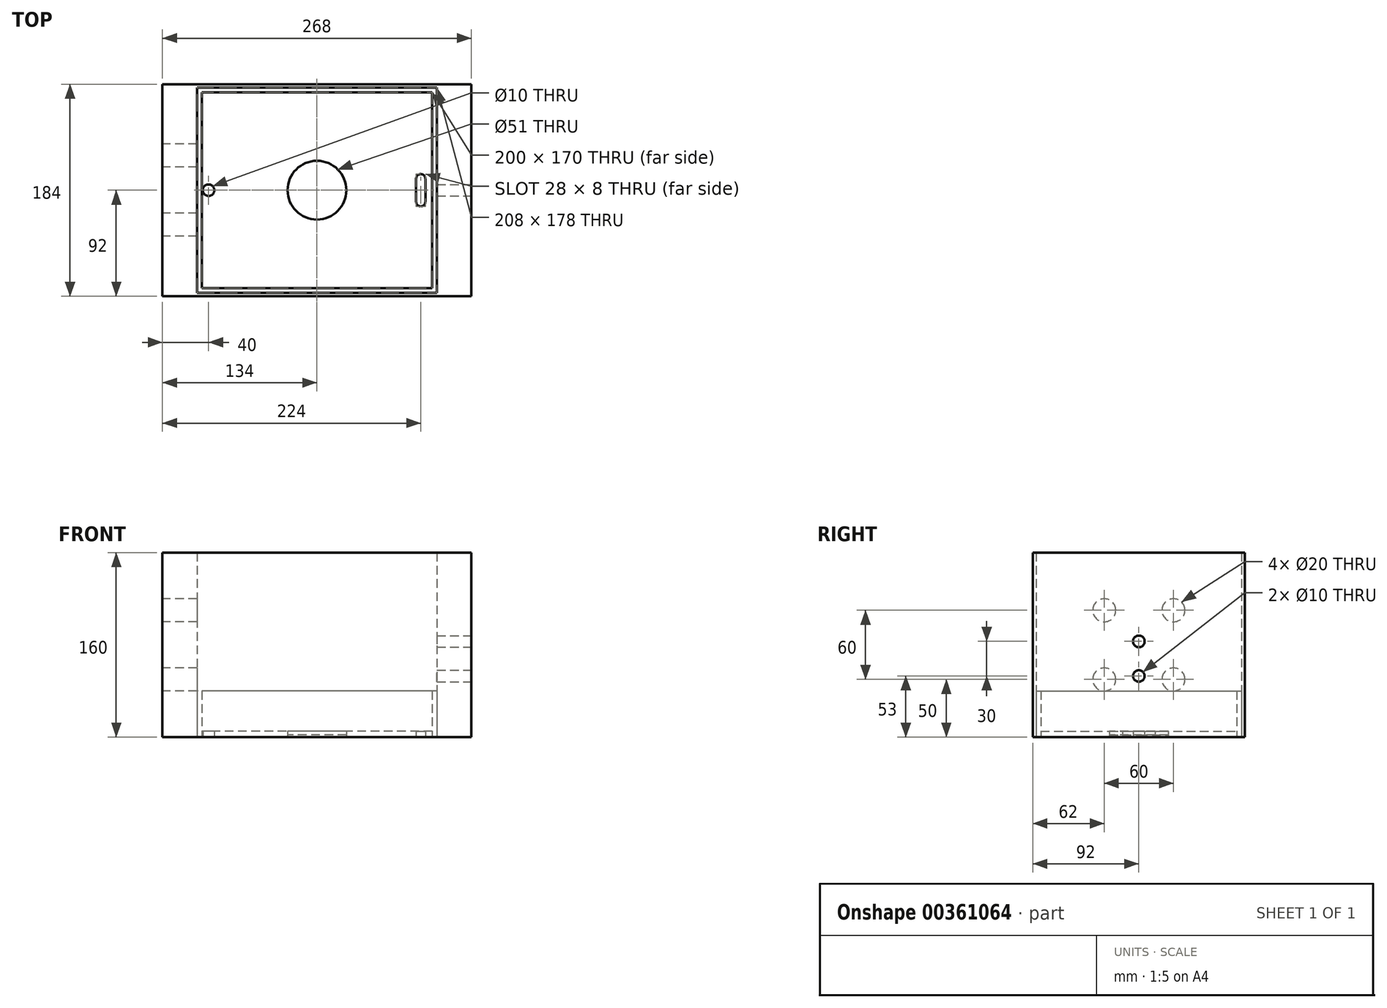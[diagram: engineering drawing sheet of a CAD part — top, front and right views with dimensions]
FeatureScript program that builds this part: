
annotation { "Feature Type Name" : "Feature", "Feature Type Description" : "" }
export const myFeature = defineFeature(function(context is Context, id is Id, definition is map)
    precondition{}
    {
        {
            var Q0;
            Q0=qCreatedBy(makeId("Top.planeOp"),FACE);
            var sketch = newSketch(context, id + "F0", { "sketchPlane" : qUnion([Q0])});
            skLineSegment(sketch, "E0.bottom", {"start": v(134, -92) * mm, "end": v(-134, -92) * mm});
            skLineSegment(sketch, "E0.top", {"start": v(134, 92) * mm, "end": v(-134, 92) * mm});
            skPoint(sketch, "E0.middle", {"position": v(0, 0) * mm});
            skCircle(sketch, "E1", {"center": v(0, 0) * mm, "radius": 25.5 * mm});
            skLineSegment(sketch, "E2.0", {"start": v(-100, -85) * mm, "end": v(-100, 85) * mm});
            skLineSegment(sketch, "E2.1", {"start": v(100, -85) * mm, "end": v(-100, -85) * mm});
            skLineSegment(sketch, "E2.2", {"start": v(100, -85) * mm, "end": v(100, 85) * mm});
            skLineSegment(sketch, "E2.3", {"start": v(100, 85) * mm, "end": v(-100, 85) * mm});
            skLineSegment(sketch, "E3.0", {"start": v(104, 89) * mm, "end": v(-104, 89) * mm});
            skLineSegment(sketch, "E3.1", {"start": v(104, -89) * mm, "end": v(104, 89) * mm});
            skLineSegment(sketch, "E3.2", {"start": v(104, -89) * mm, "end": v(-104, -89) * mm});
            skLineSegment(sketch, "E3.3", {"start": v(-104, -89) * mm, "end": v(-104, 89) * mm});
            skLineSegment(sketch, "E4", {"start": v(134, -92) * mm, "end": v(134, 92) * mm});
            skLineSegment(sketch, "E5", {"start": v(134, 0) * mm, "end": v(94, 0) * mm});
            skPoint(sketch, "E5.endSnap0", {"position": v(134, 0) * mm});
            skLineSegment(sketch, "E6", {"start": v(94, 0) * mm, "end": v(94, -10) * mm});
            skLineSegment(sketch, "E7", {"start": v(94, 0) * mm, "end": v(94, 10) * mm});
            skArc(sketch, "E8", {"start": v(94, -10) * mm, "mid": v(90, -14) * mm, "end": v(86, -10) * mm});
            skArc(sketch, "E9", {"start": v(94, 10) * mm, "mid": v(90, 14) * mm, "end": v(86, 10) * mm});
            skLineSegment(sketch, "E10", {"start": v(86, -10) * mm, "end": v(86, 10) * mm});
            skLineSegment(sketch, "E11", {"start": v(-134, 92) * mm, "end": v(-134, -92) * mm});
            skLineSegment(sketch, "E12", {"start": v(0, 0) * mm, "end": v(-100, 0) * mm, "construction": true});
            skPoint(sketch, "E13", {"position": v(-94, 0) * mm});
            skCircle(sketch, "E14", {"center": v(-94, 0) * mm, "radius": 5 * mm});
            skSolve(sketch);
        }
        {
            var Q0;
            Q0=makeQuery(id+"F0.imprint","IMPRINT",FACE,{"disambiguationData":[TD([[makeQuery(id+"F0.imprint","IMPRINT",EDGE,{"derivedFrom":sQuery(id+"F0.wireOp",EDGE,"E1")}),1.0]])]});
            extrude(context, id + "F1", {"entities" : qUnion([Q0]), "depth" : 2 * mm});
        }
        {
            var Q0;
            Q0=makeQuery(id+"F0.imprint","IMPRINT",FACE,{"disambiguationData":[TD([[makeQuery(id+"F0.imprint","IMPRINT",EDGE,{"derivedFrom":sQuery(id+"F0.wireOp",EDGE,"E1")}),-1.0]])]});
            var Q1;
            Q1=makeQuery(id+"F0.imprint","IMPRINT",FACE,{"disambiguationData":[TD([[makeQuery(id+"F0.imprint","IMPRINT",EDGE,{"derivedFrom":sQuery(id+"F0.wireOp",EDGE,"wDK2D86D-5Smb-rO2F-uM56-sWFtckQkBcLd")}),1.0]])]});
            extrude(context, id + "F2", {"entities" : qUnion([Q0, Q1]), "depth" : 5 * mm});
        }
        {
            var Q0;
            {var subQ5=sQuery(id+"F0.wireOp",EDGE,"E0.bottom");Q0=makeQuery(id+"F0.imprint","IMPRINT",FACE,{"disambiguationData":[TD([[makeQuery(id+"F0.imprint","IMPRINT",EDGE,{"derivedFrom":subQ5}),-1.0]])]});}
            extrude(context, id + "F3", {"entities" : qUnion([Q0]), "depth" : 160 * mm});
        }
        {
            var Q0;
            Q0=makeQuery(id+"F0.imprint","IMPRINT",FACE,{"disambiguationData":[TD([[makeQuery(id+"F0.imprint","IMPRINT",EDGE,{"derivedFrom":sQuery(id+"F0.wireOp",EDGE,"E2.0")}),1.0]])]});
            extrude(context, id + "F4", {"entities" : qUnion([Q0]), "depth" : 40 * mm});
        }
        {
            var Q0;
            Q0=makeQuery(id+"F3.opExtrude","SWEPT_FACE",FACE,{"disambiguationData":[OSD([sQuery(id+"F0.wireOp",EDGE,"E4")])]});
            var sketch = newSketch(context, id + "F5", { "sketchPlane" : qUnion([Q0])});
            skLineSegment(sketch, "E15", {"start": v(0, 0) * mm, "end": v(0, 35) * mm});
            skLineSegment(sketch, "E16", {"start": v(0, 35) * mm, "end": v(0, 45) * mm});
            skPoint(sketch, "E17.middle", {"position": v(0, 53) * mm});
            skPoint(sketch, "E18.middle", {"position": v(0, 83) * mm});
            skCircle(sketch, "E19", {"center": v(0, 83) * mm, "radius": 5 * mm});
            skCircle(sketch, "E20", {"center": v(0, 53) * mm, "radius": 5 * mm});
            skSolve(sketch);
        }
        {
            var Q0;
            Q0=makeQuery(id+"F5.imprint","IMPRINT",FACE,{"disambiguationData":[TD([[makeQuery(id+"F5.imprint","IMPRINT",EDGE,{"derivedFrom":sQuery(id+"F5.wireOp",EDGE,"E19")}),1.0]])]});
            extrude(context, id + "F6", {"entities" : qUnion([Q0]), "operationType" : NewBodyOperationType.REMOVE, "oppositeDirection" : true, "depth" : 30.3 * mm});
        }
        {
            var Q0;
            Q0=makeQuery(id+"F5.imprint","IMPRINT",FACE,{"disambiguationData":[TD([[makeQuery(id+"F5.imprint","IMPRINT",EDGE,{"derivedFrom":sQuery(id+"F5.wireOp",EDGE,"E20")}),1.0]])]});
            extrude(context, id + "F7", {"entities" : qUnion([Q0]), "operationType" : NewBodyOperationType.REMOVE, "oppositeDirection" : true, "depth" : 30 * mm});
        }
        {
            var Q0;
            Q0=makeQuery(id+"F0.imprint","IMPRINT",FACE,{"disambiguationData":[TD([[makeQuery(id+"F0.imprint","IMPRINT",EDGE,{"derivedFrom":sQuery(id+"F0.wireOp",EDGE,"E6")}),-1.0]])]});
            extrude(context, id + "F8", {"entities" : qUnion([Q0]), "operationType" : NewBodyOperationType.REMOVE, "depth" : 10 * mm});
        }
        {
            var Q0;
            Q0=makeQuery(id+"F3.opExtrude","SWEPT_FACE",FACE,{"disambiguationData":[OSD([sQuery(id+"F0.wireOp",EDGE,"E11")])]});
            var sketch = newSketch(context, id + "F9", { "sketchPlane" : qUnion([Q0])});
            skLineSegment(sketch, "E21", {"start": v(0, 0) * mm, "end": v(0, 160) * mm, "construction": true});
            skLineSegment(sketch, "E22", {"start": v(-92, 80) * mm, "end": v(92, 80) * mm, "construction": true});
            skPoint(sketch, "E23", {"position": v(0, 80) * mm});
            skPoint(sketch, "E24", {"position": v(0, 110) * mm});
            skPoint(sketch, "E25", {"position": v(0, 50) * mm});
            skPoint(sketch, "E26", {"position": v(30, 80) * mm});
            skPoint(sketch, "E27", {"position": v(-30, 80) * mm});
            skCircle(sketch, "E28", {"center": v(30, 50) * mm, "radius": 10 * mm});
            skCircle(sketch, "E29", {"center": v(-30, 50) * mm, "radius": 10 * mm});
            skCircle(sketch, "E30", {"center": v(-30, 110) * mm, "radius": 10 * mm});
            skCircle(sketch, "E31", {"center": v(30, 110) * mm, "radius": 10 * mm});
            skSolve(sketch);
        }
        {
            var Q0;
            Q0=makeQuery(id+"F9.imprint","IMPRINT",FACE,{"disambiguationData":[TD([[makeQuery(id+"F9.imprint","IMPRINT",EDGE,{"derivedFrom":sQuery(id+"F9.wireOp",EDGE,"E30")}),1.0]])]});
            var Q1;
            Q1=makeQuery(id+"F9.imprint","IMPRINT",FACE,{"disambiguationData":[TD([[makeQuery(id+"F9.imprint","IMPRINT",EDGE,{"derivedFrom":sQuery(id+"F9.wireOp",EDGE,"E31")}),1.0]])]});
            var Q2;
            Q2=makeQuery(id+"F9.imprint","IMPRINT",FACE,{"disambiguationData":[TD([[makeQuery(id+"F9.imprint","IMPRINT",EDGE,{"derivedFrom":sQuery(id+"F9.wireOp",EDGE,"E29")}),1.0]])]});
            var Q3;
            Q3=makeQuery(id+"F9.imprint","IMPRINT",FACE,{"disambiguationData":[TD([[makeQuery(id+"F9.imprint","IMPRINT",EDGE,{"derivedFrom":sQuery(id+"F9.wireOp",EDGE,"E28")}),1.0]])]});
            var Q4;
            Q4=makeQuery(id+"F3.opExtrude","SWEPT_FACE",FACE,{"disambiguationData":[OSD([sQuery(id+"F0.wireOp",EDGE,"E3.3")])]});
            extrude(context, id + "F10", {"entities" : qUnion([Q0, Q1, Q2, Q3]), "operationType" : NewBodyOperationType.REMOVE, "endBound" : BoundingType.UP_TO_SURFACE, "oppositeDirection" : true, "endBoundEntityFace" : qUnion([Q4]), "depth" : 25 * mm});
        }
    });
